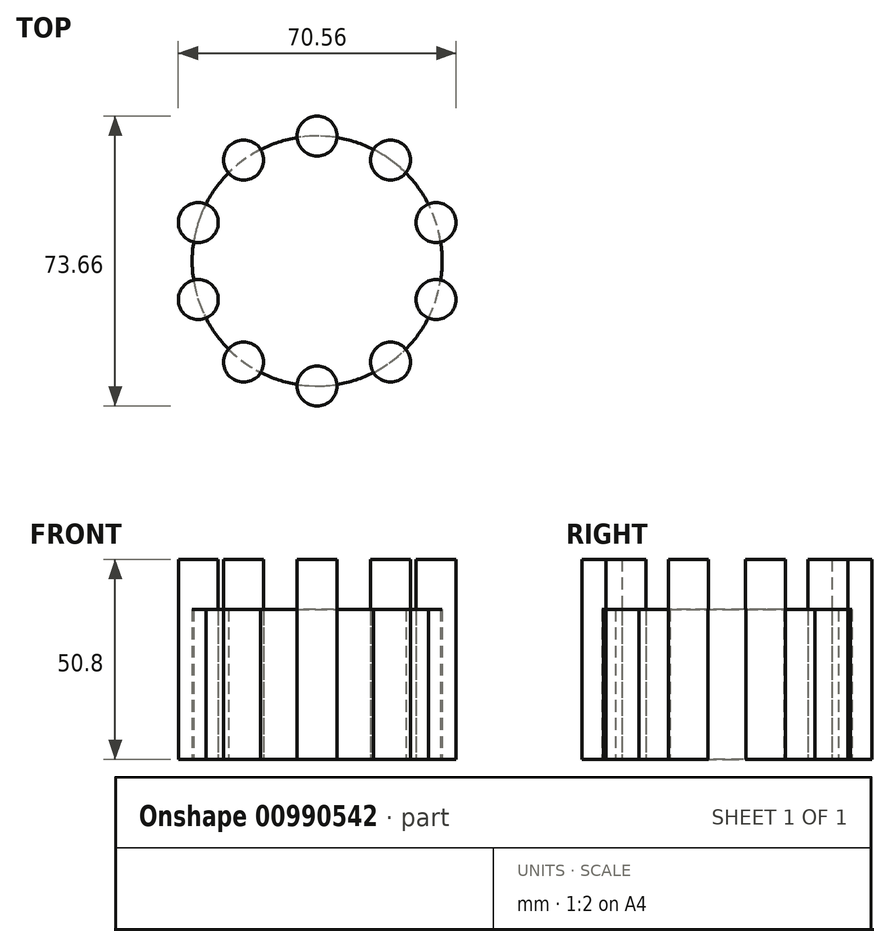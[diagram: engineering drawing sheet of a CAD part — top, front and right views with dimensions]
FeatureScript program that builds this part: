
annotation { "Feature Type Name" : "Feature", "Feature Type Description" : "" }
export const myFeature = defineFeature(function(context is Context, id is Id, definition is map)
    precondition{}
    {
        {
            var Q0;
            Q0=qCreatedBy(makeId("Top.planeOp"),FACE);
            var sketch = newSketch(context, id + "F0", { "sketchPlane" : qUnion([Q0])});
            skCircle(sketch, "E0", {"center": v(0, 0) * mm, "radius": 31.75 * mm});
            skSolve(sketch);
        }
        {
            var Q0;
            Q0=qSketchRegion(id+"F0",true);
            extrude(context, id + "F1", {"entities" : qUnion([Q0]), "depth" : 38.1 * mm});
        }
        {
            var Q0;
            Q0=qCreatedBy(makeId("Top.planeOp"),FACE);
            var sketch = newSketch(context, id + "F2", { "sketchPlane" : qUnion([Q0])});
            skCircle(sketch, "E1", {"center": v(0, 31.75) * mm, "radius": 5.08 * mm});
            skCircle(sketch, "E2.1.0", {"center": v(-18.66, 25.69) * mm, "radius": 5.08 * mm});
            skCircle(sketch, "E2.2.0", {"center": v(-30.2, 9.81) * mm, "radius": 5.08 * mm});
            skCircle(sketch, "E2.3.0", {"center": v(-30.2, -9.81) * mm, "radius": 5.08 * mm});
            skCircle(sketch, "E2.4.0", {"center": v(-18.66, -25.69) * mm, "radius": 5.08 * mm});
            skCircle(sketch, "E2.5.0", {"center": v(0, -31.75) * mm, "radius": 5.08 * mm});
            skCircle(sketch, "E2.6.0", {"center": v(18.66, -25.69) * mm, "radius": 5.08 * mm});
            skCircle(sketch, "E2.7.0", {"center": v(30.2, -9.81) * mm, "radius": 5.08 * mm});
            skCircle(sketch, "E2.8.0", {"center": v(30.2, 9.81) * mm, "radius": 5.08 * mm});
            skCircle(sketch, "E2.9.0", {"center": v(18.66, 25.69) * mm, "radius": 5.08 * mm});
            skPoint(sketch, "E2.center", {"position": v(0, 0) * mm});
            skSolve(sketch);
        }
        {
            var Q0;
            Q0=qSketchRegion(id+"F2",true);
            extrude(context, id + "F3", {"entities" : qUnion([Q0]), "offsetDistance" : 25.4 * mm, "depth" : 50.8 * mm});
        }
        {
            var Q0;
            Q0=makeQuery(id+"F3.opExtrude","SWEPT_BODY",BODY,{"disambiguationData":[OSD([sQuery(id+"F2.wireOp",EDGE,"E2.6.0")])]});
            var Q1;
            Q1=makeQuery(id+"F1.opExtrude","SWEPT_BODY",BODY,{"disambiguationData":[OSD([sQuery(id+"F0.wireOp",EDGE,"E0")])]});
            booleanBodies(context, id + "F4", {"operationType" : BooleanOperationType.INTERSECTION, "tools" : qUnion([Q0, Q1]), "keepTools" : true});
        }
        {
            var Q0;
            Q0=makeQuery(id+"F3.opExtrude","SWEPT_BODY",BODY,{"disambiguationData":[OSD([sQuery(id+"F2.wireOp",EDGE,"E2.7.0")])]});
            var Q1;
            Q1=makeQuery(id+"F1.opExtrude","SWEPT_BODY",BODY,{"disambiguationData":[OSD([sQuery(id+"F0.wireOp",EDGE,"E0")])]});
            booleanBodies(context, id + "F5", {"operationType" : BooleanOperationType.INTERSECTION, "tools" : qUnion([Q0, Q1]), "keepTools" : true});
        }
        {
            var Q0;
            Q0=makeQuery(id+"F3.opExtrude","SWEPT_BODY",BODY,{"disambiguationData":[OSD([sQuery(id+"F2.wireOp",EDGE,"E2.8.0")])]});
            var Q1;
            Q1=makeQuery(id+"F1.opExtrude","SWEPT_BODY",BODY,{"disambiguationData":[OSD([sQuery(id+"F0.wireOp",EDGE,"E0")])]});
            booleanBodies(context, id + "F6", {"operationType" : BooleanOperationType.INTERSECTION, "tools" : qUnion([Q0, Q1]), "keepTools" : true});
        }
        {
            var Q0;
            Q0=makeQuery(id+"F1.opExtrude","SWEPT_BODY",BODY,{"disambiguationData":[OSD([sQuery(id+"F0.wireOp",EDGE,"E0")])]});
            var Q1;
            Q1=makeQuery(id+"F3.opExtrude","SWEPT_BODY",BODY,{"disambiguationData":[OSD([sQuery(id+"F2.wireOp",EDGE,"E2.9.0")])]});
            booleanBodies(context, id + "F7", {"operationType" : BooleanOperationType.INTERSECTION, "tools" : qUnion([Q0, Q1]), "keepTools" : true});
        }
        {
            var Q0;
            Q0=makeQuery(id+"F3.opExtrude","SWEPT_BODY",BODY,{"disambiguationData":[OSD([sQuery(id+"F2.wireOp",EDGE,"E1")])]});
            var Q1;
            Q1=makeQuery(id+"F1.opExtrude","SWEPT_BODY",BODY,{"disambiguationData":[OSD([sQuery(id+"F0.wireOp",EDGE,"E0")])]});
            booleanBodies(context, id + "F8", {"operationType" : BooleanOperationType.INTERSECTION, "tools" : qUnion([Q0, Q1]), "keepTools" : true});
        }
        {
            var Q0;
            Q0=makeQuery(id+"F1.opExtrude","SWEPT_BODY",BODY,{"disambiguationData":[OSD([sQuery(id+"F0.wireOp",EDGE,"E0")])]});
            var Q1;
            Q1=makeQuery(id+"F3.opExtrude","SWEPT_BODY",BODY,{"disambiguationData":[OSD([sQuery(id+"F2.wireOp",EDGE,"E2.1.0")])]});
            booleanBodies(context, id + "F9", {"operationType" : BooleanOperationType.INTERSECTION, "tools" : qUnion([Q0, Q1]), "keepTools" : true});
        }
        {
            var Q0;
            Q0=makeQuery(id+"F1.opExtrude","SWEPT_BODY",BODY,{"disambiguationData":[OSD([sQuery(id+"F0.wireOp",EDGE,"E0")])]});
            var Q1;
            Q1=makeQuery(id+"F3.opExtrude","SWEPT_BODY",BODY,{"disambiguationData":[OSD([sQuery(id+"F2.wireOp",EDGE,"E2.2.0")])]});
            booleanBodies(context, id + "F10", {"operationType" : BooleanOperationType.INTERSECTION, "tools" : qUnion([Q0, Q1]), "keepTools" : true});
        }
        {
            var Q0;
            Q0=makeQuery(id+"F3.opExtrude","SWEPT_BODY",BODY,{"disambiguationData":[OSD([sQuery(id+"F2.wireOp",EDGE,"E2.3.0")])]});
            var Q1;
            Q1=makeQuery(id+"F1.opExtrude","SWEPT_BODY",BODY,{"disambiguationData":[OSD([sQuery(id+"F0.wireOp",EDGE,"E0")])]});
            booleanBodies(context, id + "F11", {"operationType" : BooleanOperationType.INTERSECTION, "tools" : qUnion([Q0, Q1]), "keepTools" : true});
        }
        {
            var Q0;
            Q0=makeQuery(id+"F3.opExtrude","SWEPT_BODY",BODY,{"disambiguationData":[OSD([sQuery(id+"F2.wireOp",EDGE,"E2.4.0")])]});
            var Q1;
            Q1=makeQuery(id+"F1.opExtrude","SWEPT_BODY",BODY,{"disambiguationData":[OSD([sQuery(id+"F0.wireOp",EDGE,"E0")])]});
            booleanBodies(context, id + "F12", {"operationType" : BooleanOperationType.INTERSECTION, "tools" : qUnion([Q0, Q1]), "keepTools" : true});
        }
        {
            var Q0;
            Q0=makeQuery(id+"F3.opExtrude","SWEPT_BODY",BODY,{"disambiguationData":[OSD([sQuery(id+"F2.wireOp",EDGE,"E2.5.0")])]});
            var Q1;
            Q1=makeQuery(id+"F1.opExtrude","SWEPT_BODY",BODY,{"disambiguationData":[OSD([sQuery(id+"F0.wireOp",EDGE,"E0")])]});
            booleanBodies(context, id + "F13", {"operationType" : BooleanOperationType.INTERSECTION, "tools" : qUnion([Q0, Q1]), "keepTools" : true});
        }
    });
